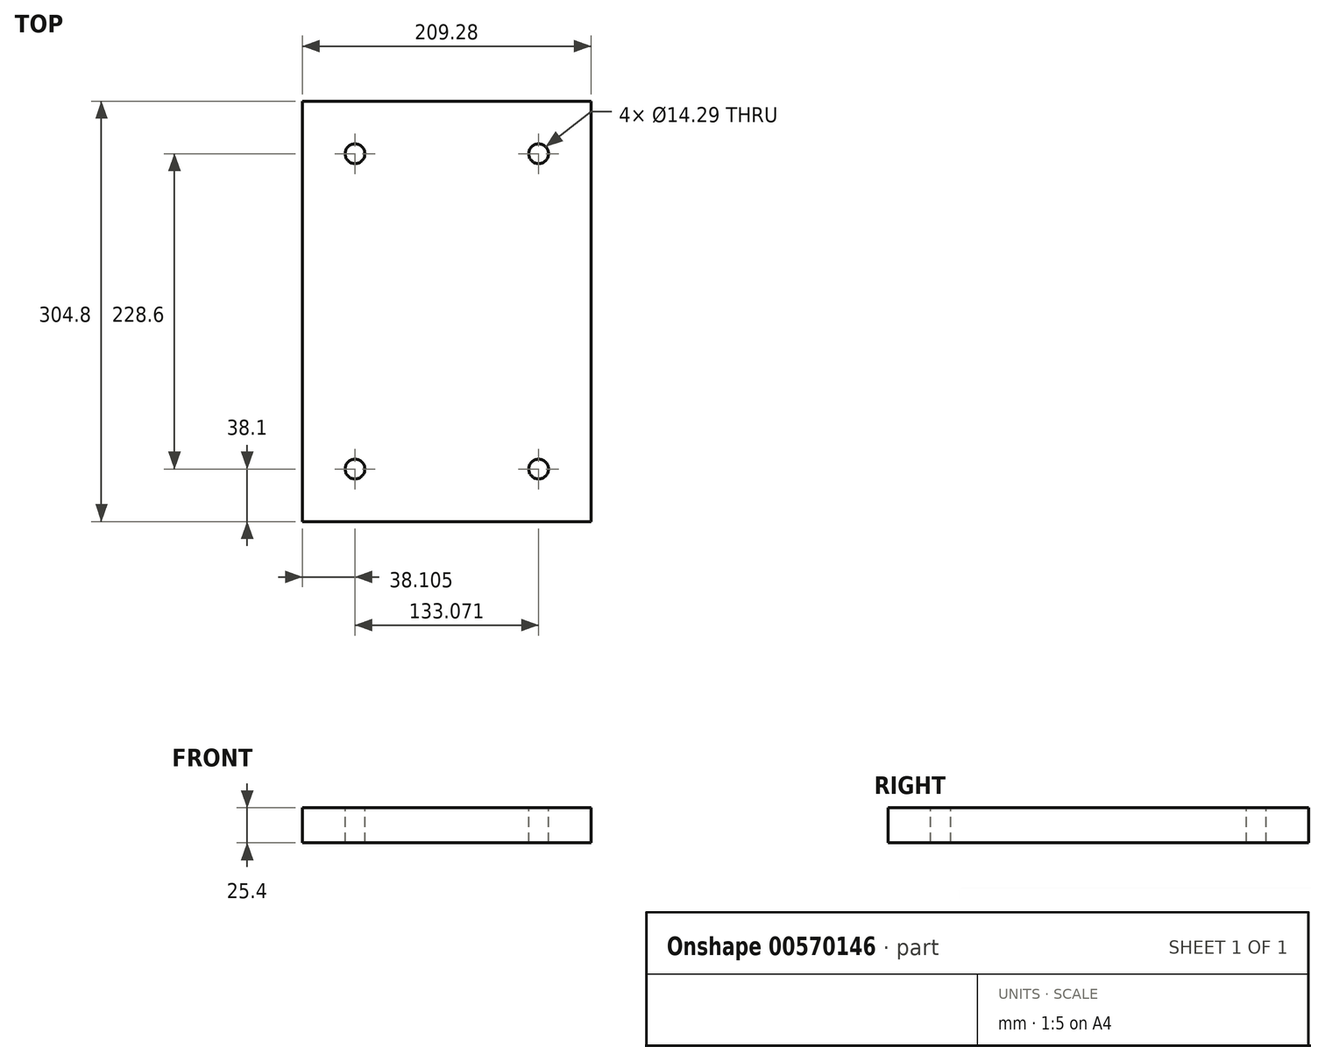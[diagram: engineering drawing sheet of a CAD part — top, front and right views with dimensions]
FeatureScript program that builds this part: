
annotation { "Feature Type Name" : "Feature", "Feature Type Description" : "" }
export const myFeature = defineFeature(function(context is Context, id is Id, definition is map)
    precondition{}
    {
        {
            var Q0;
            Q0=qCreatedBy(makeId("Top.planeOp"),FACE);
            var sketch = newSketch(context, id + "F0", { "sketchPlane" : qUnion([Q0])});
            skLineSegment(sketch, "E0.bottom", {"start": v(104.64, 152.4) * mm, "end": v(-104.64, 152.4) * mm});
            skLineSegment(sketch, "E0.top", {"start": v(104.64, -152.4) * mm, "end": v(-104.64, -152.4) * mm});
            skLineSegment(sketch, "E0.left", {"start": v(104.64, 152.4) * mm, "end": v(104.64, -152.4) * mm});
            skLineSegment(sketch, "E0.right", {"start": v(-104.64, 152.4) * mm, "end": v(-104.64, -152.4) * mm});
            skPoint(sketch, "E0.middle", {"position": v(0, 0) * mm});
            skSolve(sketch);
        }
        {
            var Q0;
            Q0=makeQuery(id+"F0.imprint","IMPRINT",FACE,{"disambiguationData":[TD([[makeQuery(id+"F0.imprint","IMPRINT",EDGE,{"derivedFrom":sQuery(id+"F0.wireOp",EDGE,"E0.bottom")}),1.0]])]});
            extrude(context, id + "F1", {"entities" : qUnion([Q0]), "depth" : 25.4 * mm, "offsetDistance" : 25.4 * mm});
        }
        {
            var Q0;
            Q0=makeQuery(id+"F1.opExtrude","CAP_FACE",FACE,{"disambiguationData":[OSD([sQuery(id+"F0.wireOp",EDGE,"E0.bottom"),sQuery(id+"F0.wireOp",EDGE,"E0.top"),sQuery(id+"F0.wireOp",EDGE,"E0.left"),sQuery(id+"F0.wireOp",EDGE,"E0.right")])],"isStart":false});
            var sketch = newSketch(context, id + "F2", { "sketchPlane" : qUnion([Q0])});
            skCircle(sketch, "E1", {"center": v(-66.54, 114.3) * mm, "radius": 7.14 * mm});
            skCircle(sketch, "E2", {"center": v(66.54, 114.3) * mm, "radius": 7.14 * mm});
            skCircle(sketch, "E3", {"center": v(66.54, -114.3) * mm, "radius": 7.14 * mm});
            skCircle(sketch, "E4", {"center": v(-66.54, -114.3) * mm, "radius": 7.14 * mm});
            skSolve(sketch);
        }
        {
            var Q0;
            Q0=makeQuery(id+"F2.imprint","IMPRINT",FACE,{"disambiguationData":[TD([[makeQuery(id+"F2.imprint","IMPRINT",EDGE,{"derivedFrom":sQuery(id+"F2.wireOp",EDGE,"E1")}),1.0]])]});
            var Q1;
            Q1=makeQuery(id+"F2.imprint","IMPRINT",FACE,{"disambiguationData":[TD([[makeQuery(id+"F2.imprint","IMPRINT",EDGE,{"derivedFrom":sQuery(id+"F2.wireOp",EDGE,"E2")}),1.0]])]});
            var Q2;
            Q2=makeQuery(id+"F2.imprint","IMPRINT",FACE,{"disambiguationData":[TD([[makeQuery(id+"F2.imprint","IMPRINT",EDGE,{"derivedFrom":sQuery(id+"F2.wireOp",EDGE,"E3")}),1.0]])]});
            var Q3;
            Q3=makeQuery(id+"F2.imprint","IMPRINT",FACE,{"disambiguationData":[TD([[makeQuery(id+"F2.imprint","IMPRINT",EDGE,{"derivedFrom":sQuery(id+"F2.wireOp",EDGE,"E4")}),1.0]])]});
            extrude(context, id + "F3", {"entities" : qUnion([Q0, Q1, Q2, Q3]), "operationType" : NewBodyOperationType.REMOVE, "endBound" : BoundingType.THROUGH_ALL, "oppositeDirection" : true, "depth" : 25.4 * mm, "offsetDistance" : 25.4 * mm});
        }
    });
